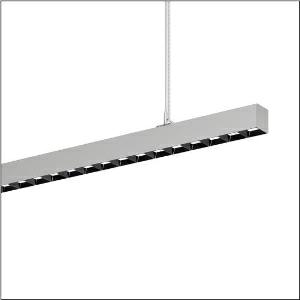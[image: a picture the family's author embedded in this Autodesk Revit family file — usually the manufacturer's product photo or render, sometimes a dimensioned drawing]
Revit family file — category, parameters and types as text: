
# Revit family: silica_r__21_51mx32dc3dsb_c9e6
name_source: partatom
category: Lighting Fixtures
units: mm (PartAtom-declared; Revit-internal decimal feet)

## family parameters
Cut with Voids When Loaded = No
Host = Face
Light Source = No
Part Type = Normal
Room Calculation Point = No
Round Connector Dimension = Use Diameter
Shared = No

## types (1)
- --- (1 x LED, 18220 lm, 113 W, 3000K)
    Apparent Load = 113 VA
    CIE Flux Codes = 86 99 100 59 100
    Color Rendering = 80
    Color Temperature = 3000K
    Default Elevation = 1800 mm
    Description = Silica® 21, office luminaire, primary light control with darklight reflector, of PMMA, black, CAT 2 (L<= 3000cd/m²), light emission: direct/indirect distribution, primary light characteristic: symmetric, installation type: suspended mounting, LED, rated luminous flux: 18.220lm, luminous efficacy: 161lm/W, light colour: 830, colour temperature: 3000K, with terminal, 3+2-pole, max. 2.5mm², mains connection: 220..240V, AC, 50/60Hz, rated input power: 113W, luminaire housing, of aluminium, metallic grey (RAL 9006), length: 3.004mm, width: 53mm, height: 53mm, protection rating (complete): IP20, insulation class (complete): insulation class I (protective earthing), certification: CE, permissible operating ambient temperature: 0..+35°C, standard: EN 50419, packaging unit: 1 piece
    Height = 53 mm
    Lamp = 1 x LED
    Lamp Light Flux = 18220 lm
    Lamp Power = 113 W
    Lamp count = 1
    Length = 3004 mm
    Luminous efficacy = 161 lm/W
    Manufacturer = Siteco
    ModVariant = No
    Model = 51MX32DC3DSB
    Mounting Place = Ceiling
    Mounting Type = Pendant
    Number of Poles = 1
    OnlyDefault = Yes
    Power Factor = 1
    Product Name = Silica® 21
    Product group = office luminaire | ceiling pendant
    ProductGroupID = 902
    Protection Class = Protection class I
    Protection Degree = IP 20
    RLX_Detail_Level = 1
    RLX_Emergency_Light_Flux = 0 lm
    RLX_Emergency_Type = 0
    RLX_Emergency_Type_DB = No
    RlxData = <blob elided: 65669 chars, md5=90ded3f8>
    Socket = socket
    Standby Power = 0 W
    System Light Flux = 18220 lm
    System Power = 113 W
    Type Comments = factory setting: luminous flux: 100 % | dim-lin: 254 | 391 mA
    Type Image = l_1297751.jpg
    URL = http://relux.com
    VarID = @adj_052637
    Voltage = 0 V
    Weight = 0.00 kg
    Width = 53 mm

## geometry (parser evidence)
native form markers: Blend x4, Sweep x11
no freeform markers — native parametric forms only
